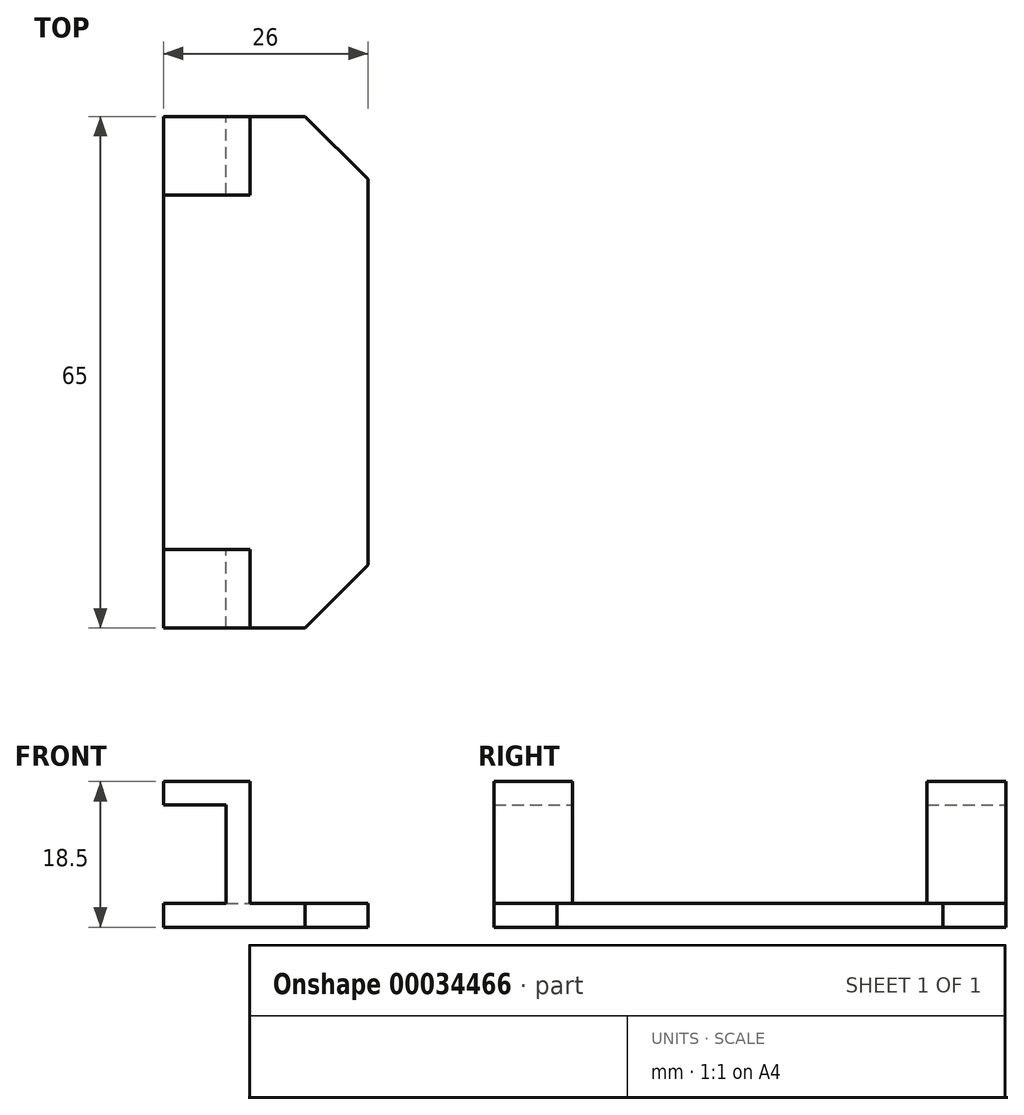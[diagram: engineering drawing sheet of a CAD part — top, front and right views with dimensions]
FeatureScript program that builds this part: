
annotation { "Feature Type Name" : "Feature", "Feature Type Description" : "" }
export const myFeature = defineFeature(function(context is Context, id is Id, definition is map)
    precondition{}
    {
        {
            var Q0;
            Q0=qCreatedBy(makeId("Front.planeOp"),FACE);
            var sketch = newSketch(context, id + "F0", { "sketchPlane" : qUnion([Q0])});
            skLineSegment(sketch, "E0", {"start": v(0, 0) * mm, "end": v(8, 0) * mm});
            skLineSegment(sketch, "E1", {"start": v(8, 0) * mm, "end": v(8, 12.5) * mm});
            skLineSegment(sketch, "E2", {"start": v(8, 12.5) * mm, "end": v(0, 12.5) * mm});
            skLineSegment(sketch, "E3", {"start": v(0, 12.5) * mm, "end": v(0, 15.5) * mm});
            skLineSegment(sketch, "E4", {"start": v(0, 15.5) * mm, "end": v(11, 15.5) * mm});
            skLineSegment(sketch, "E5", {"start": v(11, 15.5) * mm, "end": v(11, -3) * mm});
            skLineSegment(sketch, "E6", {"start": v(11, -3) * mm, "end": v(0, -3) * mm});
            skLineSegment(sketch, "E7", {"start": v(0, -3) * mm, "end": v(0, 0) * mm});
            skLineSegment(sketch, "E8", {"start": v(8, 6.25) * mm, "end": v(11, 6.25) * mm, "construction": true});
            skPoint(sketch, "E8.endSnap0", {"position": v(11, 6.25) * mm});
            skSolve(sketch);
        }
        {
            var Q0;
            Q0 = qSketchRegion(id + "F0", true);
            extrude(context, id + "F1", {"entities" : qUnion([Q0]), "endBound" : BoundingType.SYMMETRIC, "depth" : 65 * mm, "offsetDistance" : 25.4 * mm});
        }
        {
            var Q0;
            Q0=makeQuery(id+"F1.opExtrude","SWEPT_FACE",FACE,{"disambiguationData":[OSD([sQuery(id+"F0.wireOp",EDGE,"E4")])]});
            var sketch = newSketch(context, id + "F2", { "sketchPlane" : qUnion([Q0])});
            skLineSegment(sketch, "E9.bottom", {"start": v(11, 22.5) * mm, "end": v(0, 22.5) * mm});
            skLineSegment(sketch, "E9.top", {"start": v(11, -22.5) * mm, "end": v(0, -22.5) * mm});
            skLineSegment(sketch, "E9.left", {"start": v(11, 22.5) * mm, "end": v(11, -22.5) * mm});
            skLineSegment(sketch, "E9.right", {"start": v(0, 22.5) * mm, "end": v(0, -22.5) * mm});
            skLineSegment(sketch, "E10", {"start": v(0, 0) * mm, "end": v(11, 0) * mm, "construction": true});
            skPoint(sketch, "E10.startSnap0", {"position": v(0, 0) * mm});
            skSolve(sketch);
        }
        {
            var Q0;
            Q0 = qSketchRegion(id + "F2", true);
            var Q1;
            Q1=makeQuery(id+"F1.opExtrude","SWEPT_FACE",FACE,{"disambiguationData":[OSD([sQuery(id+"F0.wireOp",EDGE,"E0")])]});
            extrude(context, id + "F3", {"entities" : qUnion([Q0]), "operationType" : NewBodyOperationType.REMOVE, "endBound" : BoundingType.UP_TO_SURFACE, "oppositeDirection" : true, "depth" : 25.4 * mm, "endBoundEntityFace" : qUnion([Q1]), "offsetDistance" : 25.4 * mm});
        }
        {
            var Q0;
            Q0=makeQuery(id+"F1.opExtrude","SWEPT_FACE",FACE,{"disambiguationData":[OSD([sQuery(id+"F0.wireOp",EDGE,"E6")])]});
            var sketch = newSketch(context, id + "F4", { "sketchPlane" : qUnion([Q0])});
            skLineSegment(sketch, "E11.0", {"start": v(11, -22.5) * mm, "end": v(11, 22.5) * mm});
            skLineSegment(sketch, "E12", {"start": v(26, 32.5) * mm, "end": v(26, -32.5) * mm});
            skLineSegment(sketch, "E13", {"start": v(11, 32.5) * mm, "end": v(26, 32.5) * mm});
            skLineSegment(sketch, "E14", {"start": v(11, -32.5) * mm, "end": v(26, -32.5) * mm});
            skLineSegment(sketch, "E15", {"start": v(0, 0) * mm, "end": v(31.8, 0) * mm, "construction": true});
            skLineSegment(sketch, "E16", {"start": v(11, 22.5) * mm, "end": v(11, 32.5) * mm});
            skLineSegment(sketch, "E17", {"start": v(11, -22.5) * mm, "end": v(11, -32.5) * mm});
            skSolve(sketch);
        }
        {
            var Q0;
            Q0 = qSketchRegion(id + "F4", true);
            var Q1;
            {var subQ0=sQuery(id+"F0.wireOp",EDGE,"E0");Q1=makeQuery(id+"F3.boolean.opBoolean","MERGE",FACE,{"derivedFrom":[makeQuery(id+"F1.opExtrude","SWEPT_FACE",FACE,{"disambiguationData":[OSD([subQ0])]}),makeQuery(id+"F3.opExtrude","CAP_FACE",FACE,{"disambiguationData":[OSD([subQ0])],"isStart":false})]});}
            extrude(context, id + "F5", {"entities" : qUnion([Q0]), "operationType" : NewBodyOperationType.ADD, "endBound" : BoundingType.UP_TO_SURFACE, "oppositeDirection" : true, "depth" : 25.4 * mm, "endBoundEntityFace" : qUnion([Q1]), "offsetDistance" : 25.4 * mm});
        }
        {
            var Q0;
            Q0=makeQuery(id+"F5.opExtrude","SWEPT_EDGE",EDGE,{"disambiguationData":[OSD([sQuery(id+"F4.wireOp",EDGE,"E12"),sQuery(id+"F4.wireOp",EDGE,"E13")])]});
            var Q1;
            Q1=makeQuery(id+"F5.opExtrude","SWEPT_EDGE",EDGE,{"disambiguationData":[OSD([sQuery(id+"F4.wireOp",EDGE,"E12"),sQuery(id+"F4.wireOp",EDGE,"E14")])]});
            chamfer(context, id + "F6", {"entities" : qUnion([Q0, Q1]), "width" : 8 * mm, "tangentPropagation" : true});
        }
    });
